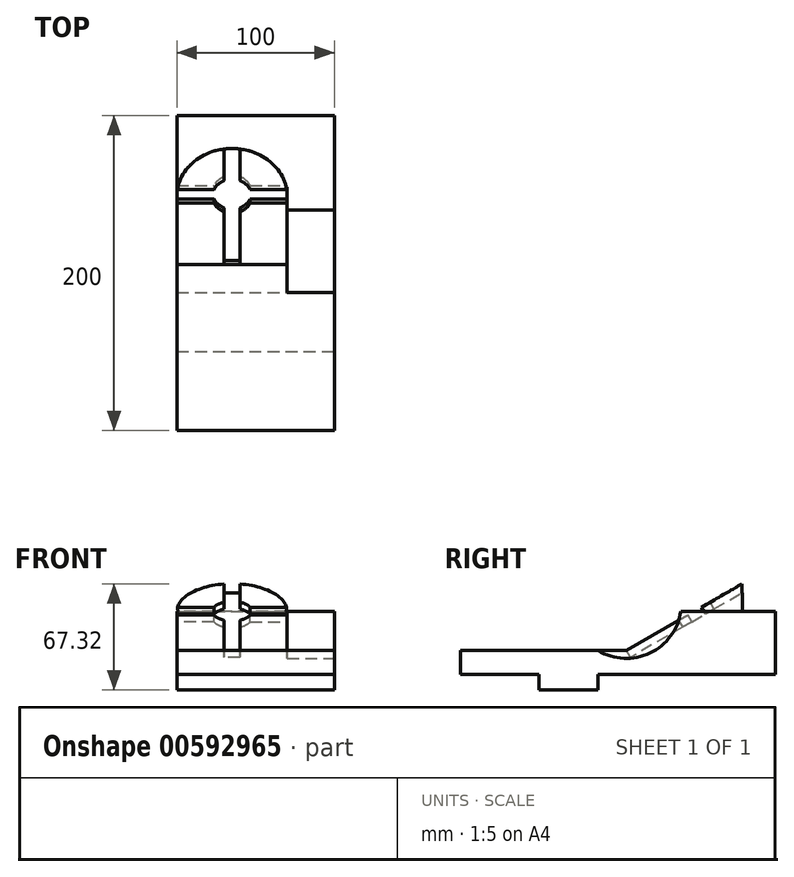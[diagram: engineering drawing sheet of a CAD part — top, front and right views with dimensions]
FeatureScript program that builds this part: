
annotation { "Feature Type Name" : "Feature", "Feature Type Description" : "" }
export const myFeature = defineFeature(function(context is Context, id is Id, definition is map)
    precondition{}
    {
        {
            var Q0;
            Q0=qCreatedBy(makeId("Right.planeOp"),FACE);
            var sketch = newSketch(context, id + "F0", { "sketchPlane" : qUnion([Q0])});
            skLineSegment(sketch, "E0", {"start": v(-100, 0) * mm, "end": v(100, 0) * mm});
            skLineSegment(sketch, "E1", {"start": v(-50, 0) * mm, "end": v(-50, -10) * mm});
            skLineSegment(sketch, "E2", {"start": v(-50, -10) * mm, "end": v(-12.5, -10) * mm});
            skLineSegment(sketch, "E3", {"start": v(-12.5, -10) * mm, "end": v(-12.5, 0) * mm});
            skLineSegment(sketch, "E4", {"start": v(12.5, 0) * mm, "end": v(12.5, -10) * mm});
            skLineSegment(sketch, "E5", {"start": v(0, 0) * mm, "end": v(0, -10.14) * mm, "construction": true});
            skLineSegment(sketch, "E6.MirrorCS", {"start": v(12.5, -10) * mm, "end": v(12.5, 0) * mm});
            skLineSegment(sketch, "E7.MirrorCS", {"start": v(50, -10) * mm, "end": v(12.5, -10) * mm});
            skLineSegment(sketch, "E8.MirrorCS", {"start": v(50, 0) * mm, "end": v(50, -10) * mm});
            skLineSegment(sketch, "E9", {"start": v(100, 0) * mm, "end": v(100, 40) * mm});
            skLineSegment(sketch, "E10", {"start": v(-100, 0) * mm, "end": v(-100, 15) * mm});
            skLineSegment(sketch, "E11", {"start": v(-100, 15) * mm, "end": v(-12.5, 15) * mm});
            skLineSegment(sketch, "E12", {"start": v(100, 40) * mm, "end": v(40, 40) * mm});
            skLineSegment(sketch, "E13", {"start": v(-15.9, 15) * mm, "end": v(-15.9, 10) * mm, "construction": true});
            skLineSegment(sketch, "E14", {"start": v(-15.9, 10) * mm, "end": v(48.4, 10) * mm, "construction": true});
            skArc(sketch, "E15", {"start": v(-12.5, 15) * mm, "mid": v(20.47, 13.39) * mm, "end": v(40, 40) * mm});
            skLineSegment(sketch, "E16", {"start": v(-12.5, 15) * mm, "end": v(23.47, 15) * mm, "construction": true});
            skSolve(sketch);
        }
        {
            var Q0;
            {var subQ6=sQuery(id+"F0.wireOp",EDGE,"E9");Q0=makeQuery(id+"F0.imprint","IMPRINT",FACE,{"disambiguationData":[TD([[makeQuery(id+"F0.imprint","IMPRINT",EDGE,{"derivedFrom":subQ6}),1.0]])]});}
            extrude(context, id + "F1", {"entities" : qUnion([Q0]), "oppositeDirection" : true, "depth" : 30 * mm, "offsetDistance" : 25 * mm});
        }
        {
            var Q0;
            {var subQ0=sQuery(id+"F0.wireOp",EDGE,"E1");Q0=makeQuery(id+"F0.imprint","IMPRINT",FACE,{"disambiguationData":[TD([[makeQuery(id+"F0.imprint","IMPRINT",EDGE,{"derivedFrom":subQ0}),1.0]])]});}
            var Q1;
            {var subQ0=sQuery(id+"F0.wireOp",EDGE,"E6.MirrorCS");Q1=makeQuery(id+"F0.imprint","IMPRINT",FACE,{"disambiguationData":[TD([[makeQuery(id+"F0.imprint","IMPRINT",EDGE,{"derivedFrom":subQ0}),-1.0]])]});}
            extrude(context, id + "F2", {"entities" : qUnion([Q0, Q1]), "operationType" : NewBodyOperationType.ADD, "oppositeDirection" : true, "depth" : 100 * mm, "offsetDistance" : 25 * mm});
        }
        {
            var Q0;
            Q0=makeQuery(id+"F1.opExtrude","CAP_FACE",FACE,{"disambiguationData":[OSD([sQuery(id+"F0.wireOp",EDGE,"E0"),sQuery(id+"F0.wireOp",EDGE,"E9"),sQuery(id+"F0.wireOp",EDGE,"E10"),sQuery(id+"F0.wireOp",EDGE,"E11"),sQuery(id+"F0.wireOp",EDGE,"E12"),sQuery(id+"F0.wireOp",EDGE,"E15")])],"isStart":false});
            var sketch = newSketch(context, id + "F3", { "sketchPlane" : qUnion([Q0])});
            skArc(sketch, "E17.0.0", {"start": v(-23.47, 15) * mm, "mid": v(-34.56, 25.63) * mm, "end": v(-40, 40) * mm});
            skLineSegment(sketch, "E17.0.1", {"start": v(-40, 40) * mm, "end": v(-100, 40) * mm});
            skLineSegment(sketch, "E17.0.2", {"start": v(-100, 40) * mm, "end": v(-100, 0) * mm});
            skLineSegment(sketch, "E17.0.3", {"start": v(-100, 0) * mm, "end": v(-50, 0) * mm});
            skLineSegment(sketch, "E17.0.4", {"start": v(-50, 0) * mm, "end": v(-12.5, 0) * mm});
            skLineSegment(sketch, "E17.0.5", {"start": v(-12.5, 0) * mm, "end": v(12.5, 0) * mm});
            skLineSegment(sketch, "E17.0.6", {"start": v(12.5, 0) * mm, "end": v(50, 0) * mm});
            skLineSegment(sketch, "E17.0.7", {"start": v(50, 0) * mm, "end": v(100, 0) * mm});
            skLineSegment(sketch, "E17.0.8", {"start": v(100, 0) * mm, "end": v(100, 15) * mm});
            skLineSegment(sketch, "E17.0.9", {"start": v(100, 15) * mm, "end": v(12.5, 15) * mm});
            skLineSegment(sketch, "E18", {"start": v(12.5, 15) * mm, "end": v(-23.47, 15) * mm});
            skSolve(sketch);
        }
        {
            var Q0;
            Q0 = qSketchRegion(id + "F3", true);
            extrude(context, id + "F4", {"entities" : qUnion([Q0]), "operationType" : NewBodyOperationType.ADD, "depth" : 70 * mm, "offsetDistance" : 25 * mm});
        }
        {
            var Q0;
            {var subQ0=sQuery(id+"F0.wireOp",EDGE,"E0");Q0=makeQuery(id+"F4.boolean.opBoolean","MERGE",FACE,{"derivedFrom":[makeQuery(id+"F2.opExtrude","CAP_FACE",FACE,{"disambiguationData":[OSD([subQ0,sQuery(id+"F0.wireOp",EDGE,"E1"),sQuery(id+"F0.wireOp",EDGE,"E2"),sQuery(id+"F0.wireOp",EDGE,"E3")])],"isStart":false}),makeQuery(id+"F2.opExtrude","CAP_FACE",FACE,{"disambiguationData":[OSD([subQ0,sQuery(id+"F0.wireOp",EDGE,"E6.MirrorCS"),sQuery(id+"F0.wireOp",EDGE,"E7.MirrorCS"),sQuery(id+"F0.wireOp",EDGE,"E8.MirrorCS")])],"isStart":false}),makeQuery(id+"F4.opExtrude","CAP_FACE",FACE,{"disambiguationData":[OSD([sQuery(id+"F3.wireOp",EDGE,"E17.0.0"),sQuery(id+"F3.wireOp",EDGE,"E17.0.1"),sQuery(id+"F3.wireOp",EDGE,"E17.0.2"),sQuery(id+"F3.wireOp",EDGE,"E17.0.3"),sQuery(id+"F3.wireOp",EDGE,"E17.0.4"),sQuery(id+"F3.wireOp",EDGE,"E17.0.5"),sQuery(id+"F3.wireOp",EDGE,"E17.0.6"),sQuery(id+"F3.wireOp",EDGE,"E17.0.7"),sQuery(id+"F3.wireOp",EDGE,"E17.0.8"),sQuery(id+"F3.wireOp",EDGE,"E17.0.9"),sQuery(id+"F3.wireOp",EDGE,"E18")])],"isStart":false})]});}
            var sketch = newSketch(context, id + "F5", { "sketchPlane" : qUnion([Q0])});
            skLineSegment(sketch, "E19.0.0", {"start": v(12.5, -10) * mm, "end": v(50, -10) * mm});
            skLineSegment(sketch, "E19.0.1", {"start": v(50, -10) * mm, "end": v(50, 0) * mm});
            skLineSegment(sketch, "E19.0.2", {"start": v(50, 0) * mm, "end": v(100, 0) * mm});
            skLineSegment(sketch, "E19.0.3", {"start": v(100, 0) * mm, "end": v(100, 15) * mm});
            skLineSegment(sketch, "E19.0.4", {"start": v(100, 15) * mm, "end": v(-23.47, 15) * mm});
            skArc(sketch, "E19.0.5", {"start": v(-23.47, 15) * mm, "mid": v(-34.56, 25.63) * mm, "end": v(-40, 40) * mm});
            skLineSegment(sketch, "E19.0.6", {"start": v(-40, 40) * mm, "end": v(-100, 40) * mm});
            skLineSegment(sketch, "E19.0.7", {"start": v(-100, 40) * mm, "end": v(-100, 0) * mm});
            skLineSegment(sketch, "E19.0.8", {"start": v(-100, 0) * mm, "end": v(-50, 0) * mm});
            skLineSegment(sketch, "E19.0.9", {"start": v(-50, 0) * mm, "end": v(-50, -10) * mm});
            skLineSegment(sketch, "E19.0.10", {"start": v(-50, -10) * mm, "end": v(-12.5, -10) * mm});
            skLineSegment(sketch, "E19.0.11", {"start": v(-12.5, -10) * mm, "end": v(-12.5, 0) * mm});
            skLineSegment(sketch, "E19.0.12", {"start": v(-12.5, 0) * mm, "end": v(12.5, 0) * mm});
            skLineSegment(sketch, "E19.0.13", {"start": v(12.5, 0) * mm, "end": v(12.5, -10) * mm});
            skLineSegment(sketch, "E20", {"start": v(-23.47, 15) * mm, "end": v(-100, 15) * mm});
            skPoint(sketch, "E21.0", {"position": v(12.5, 15) * mm});
            skLineSegment(sketch, "E22", {"start": v(-5.48, 15) * mm, "end": v(-101.82, 70.62) * mm});
            skPoint(sketch, "E23", {"position": v(-48.78, 40) * mm});
            skPoint(sketch, "E24", {"position": v(-79.1, 57.5) * mm});
            skLineSegment(sketch, "E25", {"start": v(-79.1, 57.5) * mm, "end": v(-79.1, 15) * mm});
            skSolve(sketch);
        }
        {
            var Q0;
            {var subQ0=sQuery(id+"F5.wireOp",EDGE,"E25");var subQ1=sQuery(id+"F5.wireOp",EDGE,"E19.0.6");var subQ2=makeQuery(id+"F5.imprint","INTERSECT",VERTEX,{"derivedFrom":[subQ1,subQ0]});Q0=makeQuery(id+"F5.imprint","IMPRINT",FACE,{"disambiguationData":[TD([[makeQuery(id+"F5.imprint","IMPRINT",EDGE,{"disambiguationData":[TD([[subQ2,-1.0]])],"derivedFrom":subQ1}),1.0]])]});}
            var Q1;
            {var subQ3=sQuery(id+"F5.wireOp",EDGE,"E19.0.6");var subQ7=sQuery(id+"F5.wireOp",EDGE,"E25");var subQ9=makeQuery(id+"F5.imprint","INTERSECT",VERTEX,{"derivedFrom":[subQ3,subQ7]});Q1=makeQuery(id+"F5.imprint","IMPRINT",FACE,{"disambiguationData":[TD([[makeQuery(id+"F5.imprint","IMPRINT",EDGE,{"disambiguationData":[TD([[subQ9,-1.0]])],"derivedFrom":subQ3}),-1.0]])]});}
            var Q2;
            {var subQ1=sQuery(id+"F5.wireOp",EDGE,"E19.0.4");var subQ3=sQuery(id+"F5.wireOp",EDGE,"E22");var subQ4=makeQuery(id+"F5.imprint","INTERSECT",VERTEX,{"derivedFrom":[subQ1,subQ3]});Q2=makeQuery(id+"F5.imprint","IMPRINT",FACE,{"disambiguationData":[TD([[makeQuery(id+"F5.imprint","IMPRINT",EDGE,{"disambiguationData":[TD([[subQ4,-1.0]])],"derivedFrom":subQ3}),1.0]])]});}
            extrude(context, id + "F6", {"entities" : qUnion([Q0, Q1, Q2]), "operationType" : NewBodyOperationType.ADD, "oppositeDirection" : true, "depth" : 70 * mm, "offsetDistance" : 25 * mm});
        }
        {
            var Q0;
            {var subQ0=sQuery(id+"F5.wireOp",EDGE,"E19.0.6");var subQ1=sQuery(id+"F5.wireOp",EDGE,"E19.0.5");var subQ2=makeQuery(id+"F5.imprint","INTERSECT",VERTEX,{"derivedFrom":[subQ1,subQ0]});Q0=makeQuery(id+"F5.imprint","IMPRINT",FACE,{"disambiguationData":[TD([[makeQuery(id+"F5.imprint","IMPRINT",EDGE,{"disambiguationData":[TD([[subQ2,1.0]])],"derivedFrom":subQ1}),1.0]])]});}
            extrude(context, id + "F7", {"entities" : qUnion([Q0]), "operationType" : NewBodyOperationType.REMOVE, "oppositeDirection" : true, "depth" : 70 * mm, "offsetDistance" : 25 * mm});
        }
        {
            var Q0;
            {var subQ0=sQuery(id+"F5.wireOp",EDGE,"E22");var subQ21=makeQuery(id+"F6.opExtrude","SWEPT_FACE",FACE,{"disambiguationData":[OSD([subQ0])]});Q0=makeQuery(id+"F7.boolean.opBoolean","MERGE",FACE,{"derivedFrom":[makeQuery(id+"F6.boolean.opBoolean","SPLIT",FACE,{"disambiguationData":[TD([makeQuery(id+"F1.opExtrude","SWEPT_FACE",FACE,{"disambiguationData":[OSD([sQuery(id+"F0.wireOp",EDGE,"E12")])]})])],"derivedFrom":subQ21}),makeQuery(id+"F6.boolean.opBoolean","SPLIT",FACE,{"disambiguationData":[TD([makeQuery(id+"F1.opExtrude","SWEPT_FACE",FACE,{"disambiguationData":[OSD([sQuery(id+"F0.wireOp",EDGE,"E11")])]})])],"derivedFrom":subQ21}),makeQuery(id+"F7.opExtrude","SWEPT_FACE",FACE,{"disambiguationData":[OSD([subQ0])]})]});}
            var sketch = newSketch(context, id + "F8", { "sketchPlane" : qUnion([Q0])});
            skPoint(sketch, "E26.0", {"position": v(-100, 62.24) * mm});
            skLineSegment(sketch, "E27.0.0", {"start": v(-30, 12.24) * mm, "end": v(-30, 50.56) * mm});
            skLineSegment(sketch, "E27.0.1", {"start": v(-30, 50.56) * mm, "end": v(-30, 62.24) * mm});
            skLineSegment(sketch, "E27.0.2", {"start": v(-30, 62.24) * mm, "end": v(-30, 97.24) * mm});
            skLineSegment(sketch, "E27.0.3", {"start": v(-30, 97.24) * mm, "end": v(-100, 97.24) * mm});
            skLineSegment(sketch, "E27.0.4", {"start": v(-100, 97.24) * mm, "end": v(-100, 12.24) * mm});
            skLineSegment(sketch, "E27.0.5", {"start": v(-100, 12.24) * mm, "end": v(-30, 12.24) * mm});
            skLineSegment(sketch, "E28", {"start": v(-100, 62.24) * mm, "end": v(-30, 62.24) * mm, "construction": true});
            skCircle(sketch, "E29", {"center": v(-65, 62.24) * mm, "radius": 12.5 * mm});
            skLineSegment(sketch, "E30", {"start": v(-85.94, 62.24) * mm, "end": v(-85.94, 67.24) * mm, "construction": true});
            skLineSegment(sketch, "E31", {"start": v(-85.94, 67.24) * mm, "end": v(-76.46, 67.24) * mm});
            skLineSegment(sketch, "E32", {"start": v(-85.94, 67.24) * mm, "end": v(-100, 67.24) * mm});
            skLineSegment(sketch, "E33.MirrorCS", {"start": v(-85.94, 57.24) * mm, "end": v(-76.46, 57.24) * mm});
            skLineSegment(sketch, "E34.MirrorCS", {"start": v(-85.94, 57.24) * mm, "end": v(-100, 57.24) * mm});
            skLineSegment(sketch, "E35", {"start": v(-65, 62.24) * mm, "end": v(-65, 67.24) * mm, "construction": true});
            skLineSegment(sketch, "E36", {"start": v(-60, 50.79) * mm, "end": v(-60, 12.24) * mm});
            skLineSegment(sketch, "E37", {"start": v(-70, 50.79) * mm, "end": v(-70, 12.24) * mm});
            skPoint(sketch, "E38.orphan", {"position": v(-70, 62.24) * mm});
            skPoint(sketch, "E39.start.orphan", {"position": v(-60, 62.24) * mm});
            skLineSegment(sketch, "E40.trimOffspring", {"start": v(-53.54, 57.24) * mm, "end": v(-30, 57.24) * mm});
            skLineSegment(sketch, "E41.trimOffspring", {"start": v(-53.54, 67.24) * mm, "end": v(-30, 67.24) * mm});
            skArc(sketch, "E42", {"start": v(-30.36, 57.24) * mm, "mid": v(-65, 97.24) * mm, "end": v(-99.64, 57.24) * mm});
            skPoint(sketch, "E43.start.orphan", {"position": v(-65, 67.24) * mm});
            skLineSegment(sketch, "E44.trimOffspring", {"start": v(-70, 73.7) * mm, "end": v(-70, 97.24) * mm});
            skLineSegment(sketch, "E45.trimOffspring", {"start": v(-60, 73.7) * mm, "end": v(-60, 96.89) * mm});
            skLineSegment(sketch, "E46", {"start": v(-60, 96.89) * mm, "end": v(-60, 97.24) * mm});
            skSolve(sketch);
        }
        {
            var Q0;
            {var subQ2=sQuery(id+"F8.wireOp",EDGE,"E31");Q0=makeQuery(id+"F8.imprint","IMPRINT",FACE,{"disambiguationData":[TD([[makeQuery(id+"F8.imprint","IMPRINT",EDGE,{"derivedFrom":subQ2}),-1.0]])]});}
            var Q1;
            {var subQ6=sQuery(id+"F8.wireOp",EDGE,"E45.trimOffspring");Q1=makeQuery(id+"F8.imprint","IMPRINT",FACE,{"disambiguationData":[TD([[makeQuery(id+"F8.imprint","IMPRINT",EDGE,{"derivedFrom":subQ6}),1.0]])]});}
            var Q2;
            {var subQ0=sQuery(id+"F8.wireOp",EDGE,"E36");Q2=makeQuery(id+"F8.imprint","IMPRINT",FACE,{"disambiguationData":[TD([[makeQuery(id+"F8.imprint","IMPRINT",EDGE,{"derivedFrom":subQ0}),-1.0]])]});}
            var Q3;
            {var subQ2=sQuery(id+"F8.wireOp",EDGE,"E40.trimOffspring");var subQ5=sQuery(id+"F8.wireOp",EDGE,"E29");var subQ8=makeQuery(id+"F8.imprint","INTERSECT",VERTEX,{"derivedFrom":[subQ5,subQ2]});Q3=makeQuery(id+"F8.imprint","IMPRINT",FACE,{"disambiguationData":[TD([[makeQuery(id+"F8.imprint","IMPRINT",EDGE,{"disambiguationData":[TD([[subQ8,-1.0]])],"derivedFrom":subQ5}),-1.0]])]});}
            var Q4;
            {var subQ0=sQuery(id+"F8.wireOp",EDGE,"E46");Q4=makeQuery(id+"F8.imprint","IMPRINT",FACE,{"disambiguationData":[TD([[makeQuery(id+"F8.imprint","IMPRINT",EDGE,{"derivedFrom":subQ0}),1.0]])]});}
            var Q5;
            {var subQ0=sQuery(id+"F8.wireOp",EDGE,"E44.trimOffspring");var subQ1=sQuery(id+"F8.wireOp",EDGE,"E27.0.3");var subQ2=makeQuery(id+"F8.imprint","INTERSECT",VERTEX,{"derivedFrom":[subQ1,subQ0]});Q5=makeQuery(id+"F8.imprint","IMPRINT",FACE,{"disambiguationData":[TD([[makeQuery(id+"F8.imprint","IMPRINT",EDGE,{"disambiguationData":[TD([[subQ2,1.0]])],"derivedFrom":subQ1}),1.0]])]});}
            var Q6;
            {var subQ0=sQuery(id+"F8.wireOp",EDGE,"E32");var subQ1=sQuery(id+"F8.wireOp",EDGE,"E27.0.4");var subQ2=makeQuery(id+"F8.imprint","INTERSECT",VERTEX,{"derivedFrom":[subQ1,subQ0]});Q6=makeQuery(id+"F8.imprint","IMPRINT",FACE,{"disambiguationData":[TD([[makeQuery(id+"F8.imprint","IMPRINT",EDGE,{"disambiguationData":[TD([[subQ2,1.0]])],"derivedFrom":subQ1}),-1.0]])]});}
            var Q7;
            {var subQ0=sQuery(id+"F8.wireOp",EDGE,"E34.MirrorCS");var subQ1=sQuery(id+"F8.wireOp",EDGE,"E27.0.4");var subQ2=makeQuery(id+"F8.imprint","INTERSECT",VERTEX,{"derivedFrom":[subQ1,subQ0]});Q7=makeQuery(id+"F8.imprint","IMPRINT",FACE,{"disambiguationData":[TD([[makeQuery(id+"F8.imprint","IMPRINT",EDGE,{"disambiguationData":[TD([[subQ2,-1.0]])],"derivedFrom":subQ1}),-1.0]])]});}
            var Q8;
            {var subQ1=sQuery(id+"F8.wireOp",EDGE,"E27.0.2");var subQ3=sQuery(id+"F8.wireOp",EDGE,"E41.trimOffspring");var subQ4=makeQuery(id+"F8.imprint","INTERSECT",VERTEX,{"derivedFrom":[subQ1,subQ3]});Q8=makeQuery(id+"F8.imprint","IMPRINT",FACE,{"disambiguationData":[TD([[makeQuery(id+"F8.imprint","IMPRINT",EDGE,{"disambiguationData":[TD([[subQ4,1.0]])],"derivedFrom":subQ3}),-1.0]])]});}
            var Q9;
            {var subQ1=sQuery(id+"F8.wireOp",EDGE,"E27.0.1");var subQ3=sQuery(id+"F8.wireOp",EDGE,"E40.trimOffspring");var subQ4=makeQuery(id+"F8.imprint","INTERSECT",VERTEX,{"derivedFrom":[subQ1,subQ3]});Q9=makeQuery(id+"F8.imprint","IMPRINT",FACE,{"disambiguationData":[TD([[makeQuery(id+"F8.imprint","IMPRINT",EDGE,{"disambiguationData":[TD([[subQ4,1.0]])],"derivedFrom":subQ3}),1.0]])]});}
            var Q10;
            {var subQ0=sQuery(id+"F8.wireOp",EDGE,"E29");var subQ5=makeQuery(id+"F8.imprint","INTERSECT",VERTEX,{"derivedFrom":[subQ0,sQuery(id+"F8.wireOp",EDGE,"E41.trimOffspring")]});Q10=makeQuery(id+"F8.imprint","IMPRINT",FACE,{"disambiguationData":[TD([[makeQuery(id+"F8.imprint","IMPRINT",EDGE,{"disambiguationData":[TD([[subQ5,-1.0]])],"derivedFrom":subQ0}),1.0]])]});}
            extrude(context, id + "F9", {"entities" : qUnion([Q0, Q1, Q2, Q3, Q4, Q5, Q6, Q7, Q8, Q9, Q10]), "operationType" : NewBodyOperationType.REMOVE, "oppositeDirection" : true, "depth" : 5 * mm, "offsetDistance" : 25 * mm});
        }
        {
            var Q0;
            Q0=makeQuery(id+"F4.boolean.opBoolean","MERGE",FACE,{"derivedFrom":[makeQuery(id+"F1.opExtrude","SWEPT_FACE",FACE,{"disambiguationData":[OSD([sQuery(id+"F0.wireOp",EDGE,"E12")])]}),makeQuery(id+"F4.opExtrude","SWEPT_FACE",FACE,{"disambiguationData":[OSD([sQuery(id+"F3.wireOp",EDGE,"E17.0.1")])]})]});
            cPlane(context, id + "F10", {"entities" : qUnion([Q0]), "cplaneType" : CPlaneType.OFFSET, "offset" : 17.5 * mm, "width" : 150 * mm, "height" : 150 * mm});
        }
        {
            var Q0;
            Q0=qCreatedBy(id+"F10.planeOp",FACE);
            var sketch = newSketch(context, id + "F11", { "sketchPlane" : qUnion([Q0])});
            skLineSegment(sketch, "E47.0", {"start": v(-30, 79.1) * mm, "end": v(-100, 79.1) * mm});
            skEllipticalArc(sketch, "E48.0", {});
            skLineSegment(sketch, "E49.0", {"start": v(-100, 79.1) * mm, "end": v(-100, 5.48) * mm});
            skLineSegment(sketch, "E50.0", {"start": v(-30, 48.78) * mm, "end": v(-30, 79.1) * mm});
            const initialGuessF11  = {"E48.0": [-0.065, 0.048779948322198466, -1, 0, 0.035, 0.030310889132455367, 2.998245084684426, 0.14334756890536776]};
            skSetInitialGuess(sketch, initialGuessF11);
            skSolve(sketch);
        }
        {
            var Q0;
            {var subQ0=sQuery(id+"F11.wireOp",EDGE,"E49.0");var subQ1=sQuery(id+"F11.wireOp",EDGE,"E47.0");var subQ2=makeQuery(id+"F11.imprint","INTERSECT",VERTEX,{"derivedFrom":[subQ1,subQ0]});Q0=makeQuery(id+"F11.imprint","IMPRINT",FACE,{"disambiguationData":[TD([[makeQuery(id+"F11.imprint","IMPRINT",EDGE,{"disambiguationData":[TD([[subQ2,1.0]])],"derivedFrom":subQ1}),1.0]])]});}
            var Q1;
            {var subQ0=sQuery(id+"F11.wireOp",EDGE,"E50.0");Q1=makeQuery(id+"F11.imprint","IMPRINT",FACE,{"disambiguationData":[TD([[makeQuery(id+"F11.imprint","IMPRINT",EDGE,{"derivedFrom":subQ0}),1.0]])]});}
            extrude(context, id + "F12", {"entities" : qUnion([Q0, Q1]), "operationType" : NewBodyOperationType.REMOVE, "oppositeDirection" : true, "depth" : 17.5 * mm, "offsetDistance" : 25 * mm});
        }
        {
            var Q0;
            Q0=makeQuery(id+"F4.boolean.opBoolean","MERGE",FACE,{"derivedFrom":[makeQuery(id+"F1.opExtrude","SWEPT_FACE",FACE,{"disambiguationData":[OSD([sQuery(id+"F0.wireOp",EDGE,"E10")])]}),makeQuery(id+"F4.opExtrude","SWEPT_FACE",FACE,{"disambiguationData":[OSD([sQuery(id+"F3.wireOp",EDGE,"E17.0.8")])]})]});
            cPlane(context, id + "F13", {"entities" : qUnion([Q0]), "cplaneType" : CPlaneType.OFFSET, "offset" : 15 * mm, "oppositeDirection" : true, "width" : 150 * mm, "height" : 150 * mm});
        }
    });
